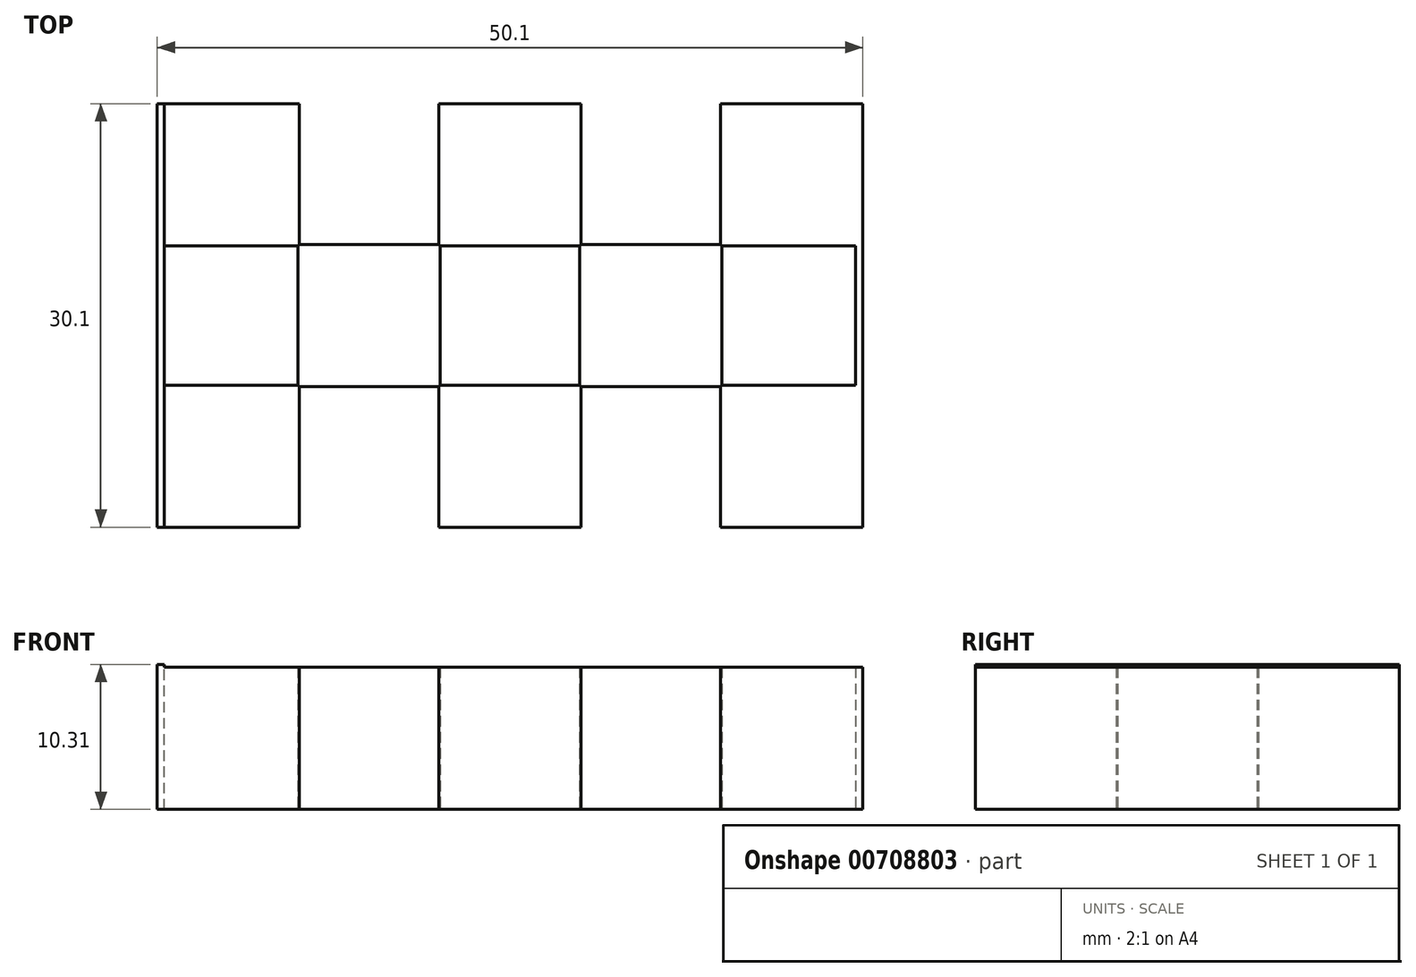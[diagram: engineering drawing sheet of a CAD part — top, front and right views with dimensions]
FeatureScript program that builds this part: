
annotation { "Feature Type Name" : "Feature", "Feature Type Description" : "" }
export const myFeature = defineFeature(function(context is Context, id is Id, definition is map)
    precondition{}
    {
        {
            var Q0;
            Q0=qCreatedBy(makeId("Top.planeOp"),FACE);
            var sketch = newSketch(context, id + "F0", { "sketchPlane" : qUnion([Q0])});
            skLineSegment(sketch, "E0.bottom", {"start": v(0, 0) * mm, "end": v(10.1, 0) * mm});
            skLineSegment(sketch, "E0.top", {"start": v(0, 10.1) * mm, "end": v(10.1, 10.1) * mm});
            skLineSegment(sketch, "E0.left", {"start": v(0, 0) * mm, "end": v(0, 10.1) * mm});
            skLineSegment(sketch, "E0.right", {"start": v(10.1, 0) * mm, "end": v(10.1, 10.1) * mm});
            skSolve(sketch);
        }
        {
            var Q0;
            Q0=makeQuery(id+"F0.imprint","IMPRINT",FACE,{"disambiguationData":[TD([[makeQuery(id+"F0.imprint","IMPRINT",EDGE,{"derivedFrom":sQuery(id+"F0.wireOp",EDGE,"E0.bottom")}),1.0]])]});
            extrude(context, id + "F1", {"entities" : qUnion([Q0]), "depth" : 10.1 * mm, "offsetDistance" : 25 * mm});
        }
        {
            var Q0;
            Q0=makeQuery(id+"F1.opExtrude","SWEPT_BODY",BODY,{"disambiguationData":[OSD([sQuery(id+"F0.wireOp",EDGE,"E0.bottom"),sQuery(id+"F0.wireOp",EDGE,"E0.top"),sQuery(id+"F0.wireOp",EDGE,"E0.left"),sQuery(id+"F0.wireOp",EDGE,"E0.right")])]});
            transform(context, id + "F2", {"entities" : qUnion([Q0]), "transformType" : TransformType.TRANSLATION_3D, "dx" : 20 * mm, "dy" : 0 * mm, "dz" : 0 * mm, "makeCopy" : true});
        }
        {
            var Q0;
            Q0=makeQuery(id+"F2.opPattern","COPY",BODY,{"derivedFrom":makeQuery(id+"F1.opExtrude","SWEPT_BODY",BODY,{"disambiguationData":[OSD([sQuery(id+"F0.wireOp",EDGE,"E0.bottom"),sQuery(id+"F0.wireOp",EDGE,"E0.top"),sQuery(id+"F0.wireOp",EDGE,"E0.left"),sQuery(id+"F0.wireOp",EDGE,"E0.right")])]}),"instanceName":"1"});
            transform(context, id + "F3", {"entities" : qUnion([Q0]), "transformType" : TransformType.TRANSLATION_3D, "dx" : 20 * mm, "dy" : 0 * mm, "dz" : 0 * mm, "makeCopy" : true});
        }
        {
            var Q0;
            Q0=makeQuery(id+"F1.opExtrude","SWEPT_BODY",BODY,{"disambiguationData":[OSD([sQuery(id+"F0.wireOp",EDGE,"E0.bottom"),sQuery(id+"F0.wireOp",EDGE,"E0.top"),sQuery(id+"F0.wireOp",EDGE,"E0.left"),sQuery(id+"F0.wireOp",EDGE,"E0.right")])]});
            transform(context, id + "F4", {"entities" : qUnion([Q0]), "transformType" : TransformType.TRANSLATION_3D, "dx" : 10 * mm, "dy" : 10 * mm, "dz" : 0 * mm, "makeCopy" : true});
        }
        {
            var Q0;
            Q0=makeQuery(id+"F2.opPattern","COPY",BODY,{"derivedFrom":makeQuery(id+"F1.opExtrude","SWEPT_BODY",BODY,{"disambiguationData":[OSD([sQuery(id+"F0.wireOp",EDGE,"E0.bottom"),sQuery(id+"F0.wireOp",EDGE,"E0.top"),sQuery(id+"F0.wireOp",EDGE,"E0.left"),sQuery(id+"F0.wireOp",EDGE,"E0.right")])]}),"instanceName":"1"});
            transform(context, id + "F5", {"entities" : qUnion([Q0]), "transformType" : TransformType.TRANSLATION_3D, "dx" : 10 * mm, "dy" : 10 * mm, "dz" : 0 * mm, "makeCopy" : true});
        }
        {
            var Q0;
            Q0=makeQuery(id+"F4.opPattern","COPY",BODY,{"derivedFrom":makeQuery(id+"F1.opExtrude","SWEPT_BODY",BODY,{"disambiguationData":[OSD([sQuery(id+"F0.wireOp",EDGE,"E0.bottom"),sQuery(id+"F0.wireOp",EDGE,"E0.top"),sQuery(id+"F0.wireOp",EDGE,"E0.left"),sQuery(id+"F0.wireOp",EDGE,"E0.right")])]}),"instanceName":"1"});
            transform(context, id + "F6", {"entities" : qUnion([Q0]), "transformType" : TransformType.TRANSLATION_3D, "dx" : -10 * mm, "dy" : 10 * mm, "dz" : 0 * mm, "makeCopy" : true});
        }
        {
            var Q0;
            Q0=makeQuery(id+"F4.opPattern","COPY",BODY,{"derivedFrom":makeQuery(id+"F1.opExtrude","SWEPT_BODY",BODY,{"disambiguationData":[OSD([sQuery(id+"F0.wireOp",EDGE,"E0.bottom"),sQuery(id+"F0.wireOp",EDGE,"E0.top"),sQuery(id+"F0.wireOp",EDGE,"E0.left"),sQuery(id+"F0.wireOp",EDGE,"E0.right")])]}),"instanceName":"1"});
            transform(context, id + "F7", {"entities" : qUnion([Q0]), "transformType" : TransformType.TRANSLATION_3D, "dx" : 10 * mm, "dy" : 10 * mm, "dz" : 0 * mm, "makeCopy" : true});
        }
        {
            var Q0;
            Q0=makeQuery(id+"F5.opPattern","COPY",BODY,{"derivedFrom":makeQuery(id+"F2.opPattern","COPY",BODY,{"derivedFrom":makeQuery(id+"F1.opExtrude","SWEPT_BODY",BODY,{"disambiguationData":[OSD([sQuery(id+"F0.wireOp",EDGE,"E0.bottom"),sQuery(id+"F0.wireOp",EDGE,"E0.top"),sQuery(id+"F0.wireOp",EDGE,"E0.left"),sQuery(id+"F0.wireOp",EDGE,"E0.right")])]}),"instanceName":"1"}),"instanceName":"1"});
            transform(context, id + "F8", {"entities" : qUnion([Q0]), "transformType" : TransformType.TRANSLATION_3D, "dx" : 10 * mm, "dy" : 10 * mm, "dz" : 0 * mm, "makeCopy" : true});
        }
        {
            var Q0;
            Q0=makeQuery(id+"F6.opPattern","COPY",FACE,{"derivedFrom":makeQuery(id+"F4.opPattern","COPY",FACE,{"derivedFrom":makeQuery(id+"F1.opExtrude","SWEPT_FACE",FACE,{"disambiguationData":[OSD([sQuery(id+"F0.wireOp",EDGE,"E0.left")])]}),"instanceName":"1"}),"instanceName":"1"});
            var sketch = newSketch(context, id + "F9", { "sketchPlane" : qUnion([Q0])});
            skLineSegment(sketch, "E1.bottom", {"start": v(-30.1, 0) * mm, "end": v(0, 0) * mm});
            skLineSegment(sketch, "E1.top", {"start": v(-30.1, 10.31) * mm, "end": v(0, 10.31) * mm});
            skLineSegment(sketch, "E1.left", {"start": v(-30.1, 0) * mm, "end": v(-30.1, 10.31) * mm});
            skLineSegment(sketch, "E1.right", {"start": v(0, 0) * mm, "end": v(0, 10.31) * mm});
            skSolve(sketch);
        }
        {
            var Q0;
            Q0 = qSketchRegion(id + "F9", true);
            extrude(context, id + "F10", {"entities" : qUnion([Q0]), "operationType" : NewBodyOperationType.ADD, "oppositeDirection" : true, "depth" : .5 * mm, "offsetDistance" : 25 * mm});
        }
        {
            var Q0;
            Q0=makeQuery(id+"F8.opPattern","COPY",FACE,{"derivedFrom":makeQuery(id+"F5.opPattern","COPY",FACE,{"derivedFrom":makeQuery(id+"F2.opPattern","COPY",FACE,{"derivedFrom":makeQuery(id+"F1.opExtrude","SWEPT_FACE",FACE,{"disambiguationData":[OSD([sQuery(id+"F0.wireOp",EDGE,"E0.right")])]}),"instanceName":"1"}),"instanceName":"1"}),"instanceName":"1"});
            var sketch = newSketch(context, id + "F11", { "sketchPlane" : qUnion([Q0])});
            skLineSegment(sketch, "E2.bottom", {"start": v(30.1, 10.1) * mm, "end": v(0, 10.1) * mm});
            skLineSegment(sketch, "E2.top", {"start": v(30.1, 0) * mm, "end": v(0, 0) * mm});
            skLineSegment(sketch, "E2.left", {"start": v(30.1, 10.1) * mm, "end": v(30.1, 0) * mm});
            skLineSegment(sketch, "E2.right", {"start": v(0, 10.1) * mm, "end": v(0, 0) * mm});
            skSolve(sketch);
        }
        {
            var Q0;
            Q0 = qSketchRegion(id + "F11", true);
            extrude(context, id + "F12", {"entities" : qUnion([Q0]), "operationType" : NewBodyOperationType.ADD, "oppositeDirection" : true, "depth" : .5 * mm, "offsetDistance" : 25 * mm});
        }
    });
